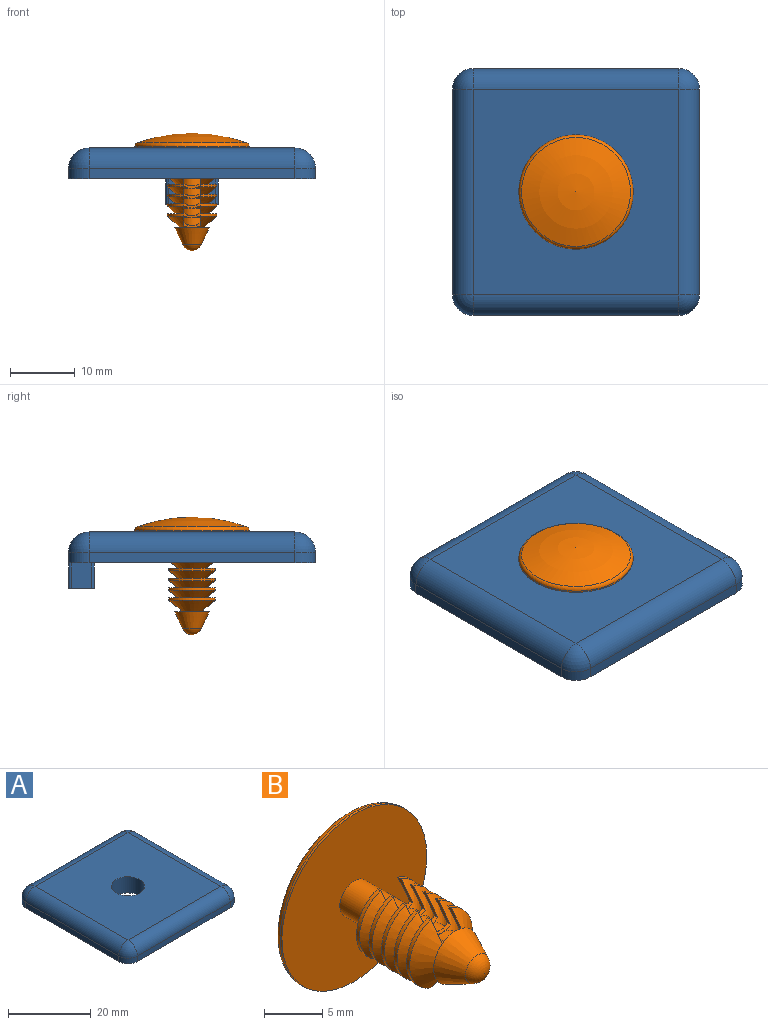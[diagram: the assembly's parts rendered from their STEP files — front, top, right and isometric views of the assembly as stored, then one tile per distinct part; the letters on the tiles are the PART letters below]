
ASSEMBLY  parts=2 mates=1
PART A: 27 faces, bbox 38.1x38.1x8.7 mm
  f0: sphere r=3.17mm, area 15.8mm2, adj f1,f3,f19
  f1: cylinder r=3.17mm len=3.18mm, axis (0,0,1), area 8mm2, adj f0,f2,f4,f18
  f2: plane 31.75x5.56mm, normal (0,1,0), area 79.6mm2, adj f1,f3,f4,f6,f11,f25,f26
  f3: cylinder r=3.17mm len=31.75mm, axis (1,0,0), area 158.3mm2, adj f0,f2,f7,f10
  f4: plane 38.1x38.1mm, normal (0,0,-1), area 1361.3mm2, adj f1,f2,f5,f6,f8,f11,f12,f14
  f5: cylinder r=3.99mm len=7.98mm, axis (0,0,1), area 119.6mm2, adj f4,f7
  f6: cylinder r=0.38mm len=3.96mm, axis (0,0,-1), area 2.4mm2, adj f2,f4,f20,f26
  f7: plane 31.75x31.75mm, normal (0,0,1), area 958.1mm2, adj f3,f5,f9,f15,f19
  f8: plane 31.75x1.6mm, normal (-1,0,0), area 50.8mm2, adj f4,f9,f11,f12
  f9: cylinder r=3.17mm len=31.75mm, axis (0,1,0), area 158.3mm2, adj f7,f8,f10,f13
  f10: sphere r=3.17mm, area 15.8mm2, adj f3,f9,f11
  f11: cylinder r=3.17mm len=3.18mm, axis (0,0,-1), area 8mm2, adj f2,f4,f8,f10
  f12: cylinder r=3.17mm len=3.18mm, axis (0,0,1), area 8mm2, adj f4,f8,f13,f14
  f13: sphere r=3.17mm, area 15.8mm2, adj f9,f12,f15
  f14: plane 31.75x1.6mm, normal (0,-1,0), area 50.8mm2, adj f4,f12,f15,f16
  f15: cylinder r=3.17mm len=31.75mm, axis (-1,0,0), area 158.3mm2, adj f7,f13,f14,f17
  f16: cylinder r=3.17mm len=3.18mm, axis (0,0,1), area 8mm2, adj f4,f14,f17,f18
  f17: sphere r=3.17mm, area 15.8mm2, adj f15,f16,f19
  f18: plane 31.75x1.6mm, normal (1,0,0), area 50.8mm2, adj f1,f4,f16,f19
  f19: cylinder r=3.17mm len=31.75mm, axis (0,-1,0), area 158.3mm2, adj f0,f7,f17,f18
  f20: plane 3.96x3.2mm, normal (-1,0,0), area 12.7mm2, adj f4,f6,f21,f26
  f21: cylinder r=0.38mm len=3.96mm, axis (0,0,-1), area 2.4mm2, adj f4,f20,f22,f26
  f22: plane 7.26x3.96mm, normal (0,-1,0), area 28.8mm2, adj f4,f21,f23,f26
  f23: cylinder r=0.38mm len=3.96mm, axis (0,0,-1), area 2.4mm2, adj f4,f22,f24,f26
  f24: plane 3.96x3.2mm, normal (1,0,0), area 12.7mm2, adj f4,f23,f25,f26
  f25: cylinder r=0.38mm len=3.96mm, axis (0,0,-1), area 2.4mm2, adj f2,f4,f24,f26
  f26: plane 8.03x3.96mm, normal (0,0,-1), area 31.7mm2, adj f2,f6,f20,f21,f22,f23,f24,f25
PART B: 72 faces, bbox 19.4x18.4x19.4 mm
  f0: plane 2.07x2.06mm, normal (-1,0,0), area 0.7mm2, adj f1,f2,f16,f59
  f1: cone r=3.81mm half-angle=48.8deg, axis (0,1,0), area 17.1mm2, adj f0,f6,f8,f16,f45,f59
  f2: cone r=1.78mm half-angle=48.8deg, axis (0,1,0), area 17.1mm2, adj f0,f6,f7,f16,f45,f59
  f3: cone r=3.81mm half-angle=48.8deg, axis (0,1,0), area 17.1mm2, adj f26,f27,f32,f33,f46,f47
  f4: cone r=3.81mm half-angle=48.8deg, axis (0,1,0), area 17.1mm2, adj f23,f25,f35,f36,f49,f50
  f5: cone r=3.81mm half-angle=48.8deg, axis (0,1,0), area 17.1mm2, adj f20,f22,f38,f39,f52,f53
  f6: plane 2.07x2.06mm, normal (-1,0,0), area 0.7mm2, adj f1,f2,f16,f45
  f7: cylinder r=1.78mm len=3.56mm, axis (0,1,0), area 12.8mm2, adj f2,f13,f19,f62
  f8: cylinder r=1.78mm len=5.84mm, axis (0,1,0), area 65.3mm2, adj f1,f9,f15
  f9: plane 17.65x17.65mm, normal (0,-1,0), area 234.8mm2, adj f8,f10
  f10: cylinder r=8.83mm len=17.65mm, axis (0,1,0), area 12.1mm2, adj f9,f11
  f11: torus R=8.19mm, axis (0,-1,0), area 42.4mm2, adj f10,f12
  f12: sphere r=24.77mm, area 228.8mm2, adj f11
  f13: cone r=1.78mm half-angle=48.8deg, axis (0,1,0), area 17.1mm2, adj f7,f14,f44,f45,f58,f59
  f14: cylinder r=3.81mm len=7.2mm, axis (0,-1,0), area 3.6mm2, adj f13,f15,f44,f58
  f15: cone r=3.81mm half-angle=48.8deg, axis (0,1,0), area 17.1mm2, adj f8,f14,f44,f45,f58,f59
  f16: cylinder r=3.81mm len=7.2mm, axis (0,-1,0), area 3.6mm2, adj f0,f1,f2,f6
  f17: cone r=1.78mm half-angle=48.8deg, axis (0,1,0), area 17.1mm2, adj f18,f20,f41,f42,f55,f56
  f18: cylinder r=3.81mm len=7.2mm, axis (0,-1,0), area 3.6mm2, adj f17,f19,f41,f56
  f19: cone r=3.81mm half-angle=48.8deg, axis (0,1,0), area 17.1mm2, adj f7,f18,f41,f42,f55,f56
  f20: cylinder r=1.78mm len=3.56mm, axis (0,1,0), area 12.8mm2, adj f5,f17,f64,f65
  f21: cone r=1.78mm half-angle=48.8deg, axis (0,1,0), area 17.1mm2, adj f22,f23,f38,f39,f52,f53
  f22: cylinder r=3.81mm len=7.2mm, axis (0,-1,0), area 3.6mm2, adj f5,f21,f38,f53
  f23: cylinder r=1.78mm len=3.56mm, axis (0,1,0), area 12.8mm2, adj f4,f21,f60,f68
  f24: cone r=1.78mm half-angle=48.8deg, axis (0,1,0), area 17.1mm2, adj f25,f26,f35,f36,f49,f50
  f25: cylinder r=3.81mm len=7.2mm, axis (0,-1,0), area 3.6mm2, adj f4,f24,f35,f50
  f26: cylinder r=1.78mm len=3.56mm, axis (0,1,0), area 12.8mm2, adj f3,f24,f66,f69
  f27: cylinder r=3.81mm len=7.2mm, axis (0,-1,0), area 3.6mm2, adj f3,f28,f32,f47
  f28: cone r=1.78mm half-angle=48.8deg, axis (0,1,0), area 17.1mm2, adj f27,f31,f32,f33,f46,f47
  f29: sphere r=1.57mm, area 9mm2, adj f30
  f30: cone r=2.67mm half-angle=25.1deg, axis (0,1,0), area 37.6mm2, adj f29,f31
  f31: plane 5.33x5.33mm, normal (0,1,0), area 12.4mm2, adj f28,f30,f71
  f32: plane 2.07x2.06mm, normal (-1,0,0), area 0.7mm2, adj f3,f27,f28,f33
  f33: plane 2.76x1mm, normal (0,0,-1), area 0.9mm2, adj f3,f28,f32,f34,f69,f71
  f34: plane 2.07x2.06mm, normal (1,0,0), area 0.7mm2, adj f33,f69,f70,f71
  f35: plane 2.07x2.06mm, normal (-1,0,0), area 0.7mm2, adj f4,f24,f25,f36
  f36: plane 2.76x1mm, normal (0,0,-1), area 0.9mm2, adj f4,f24,f35,f37,f66,f68
  f37: plane 2.07x2.06mm, normal (1,0,0), area 0.7mm2, adj f36,f66,f67,f68
  f38: plane 2.07x2.06mm, normal (-1,0,0), area 0.7mm2, adj f5,f21,f22,f39
  f39: plane 2.76x1mm, normal (0,0,-1), area 0.9mm2, adj f5,f21,f38,f40,f60,f65
  f40: plane 2.07x2.06mm, normal (1,0,0), area 0.7mm2, adj f39,f60,f61,f65
  f41: plane 2.07x2.06mm, normal (-1,0,0), area 0.7mm2, adj f17,f18,f19,f42
  f42: plane 2.76x1mm, normal (0,0,-1), area 0.9mm2, adj f17,f19,f41,f43,f62,f64
  f43: plane 2.07x2.06mm, normal (1,0,0), area 0.7mm2, adj f42,f62,f63,f64
  f44: plane 2.07x2.06mm, normal (1,0,0), area 0.7mm2, adj f13,f14,f15,f45
  f45: plane 2.76x1mm, normal (0,0,-1), area 0.9mm2, adj f1,f2,f6,f13,f15,f44
  f46: plane 2.76x1mm, normal (0,0,1), area 0.9mm2, adj f3,f28,f47,f48,f69,f71
  f47: plane 2.07x2.06mm, normal (-1,0,0), area 0.7mm2, adj f3,f27,f28,f46
  f48: plane 2.07x2.06mm, normal (1,0,0), area 0.7mm2, adj f46,f69,f70,f71
  f49: plane 2.76x1mm, normal (0,0,1), area 0.9mm2, adj f4,f24,f50,f51,f66,f68
  f50: plane 2.07x2.06mm, normal (-1,0,0), area 0.7mm2, adj f4,f24,f25,f49
  f51: plane 2.07x2.06mm, normal (1,0,0), area 0.7mm2, adj f49,f66,f67,f68
  f52: plane 2.76x1mm, normal (0,0,1), area 0.9mm2, adj f5,f21,f53,f54,f60,f65
  f53: plane 2.07x2.06mm, normal (-1,0,0), area 0.7mm2, adj f5,f21,f22,f52
  f54: plane 2.07x2.06mm, normal (1,0,0), area 0.7mm2, adj f52,f60,f61,f65
  f55: plane 2.76x1mm, normal (0,0,1), area 0.9mm2, adj f17,f19,f56,f57,f62,f64
  f56: plane 2.07x2.06mm, normal (-1,0,0), area 0.7mm2, adj f17,f18,f19,f55
  f57: plane 2.07x2.06mm, normal (1,0,0), area 0.7mm2, adj f55,f62,f63,f64
  f58: plane 2.07x2.06mm, normal (1,0,0), area 0.7mm2, adj f13,f14,f15,f59
  f59: plane 2.76x1mm, normal (0,0,1), area 0.9mm2, adj f0,f1,f2,f13,f15,f58
  f60: cone r=1.78mm half-angle=48.8deg, axis (0,1,0), area 17.1mm2, adj f23,f39,f40,f52,f54,f61
  f61: cylinder r=3.81mm len=7.2mm, axis (0,-1,0), area 3.6mm2, adj f40,f54,f60,f65
  f62: cone r=3.81mm half-angle=48.8deg, axis (0,1,0), area 17.1mm2, adj f7,f42,f43,f55,f57,f63
  f63: cylinder r=3.81mm len=7.2mm, axis (0,-1,0), area 3.6mm2, adj f43,f57,f62,f64
  f64: cone r=1.78mm half-angle=48.8deg, axis (0,1,0), area 17.1mm2, adj f20,f42,f43,f55,f57,f63
  f65: cone r=3.81mm half-angle=48.8deg, axis (0,1,0), area 17.1mm2, adj f20,f39,f40,f52,f54,f61
  f66: cone r=1.78mm half-angle=48.8deg, axis (0,1,0), area 17.1mm2, adj f26,f36,f37,f49,f51,f67
  f67: cylinder r=3.81mm len=7.2mm, axis (0,-1,0), area 3.6mm2, adj f37,f51,f66,f68
  f68: cone r=3.81mm half-angle=48.8deg, axis (0,1,0), area 17.1mm2, adj f23,f36,f37,f49,f51,f67
  f69: cone r=3.81mm half-angle=48.8deg, axis (0,1,0), area 17.1mm2, adj f26,f33,f34,f46,f48,f70
  f70: cylinder r=3.81mm len=7.2mm, axis (0,-1,0), area 3.6mm2, adj f34,f48,f69,f71
  f71: cone r=1.78mm half-angle=48.8deg, axis (0,1,0), area 17.1mm2, adj f31,f33,f34,f46,f48,f70
PLACE A t=(20.45,4.5,-10.95)mm
PLACE B rot(axis=(1,0,0),90deg) t=(20.45,4.5,-10.95)mm
MATE fastened B.f1 <-> A.f5  axis (0,0,1) through (20.45,4.5,-10.95)mm
